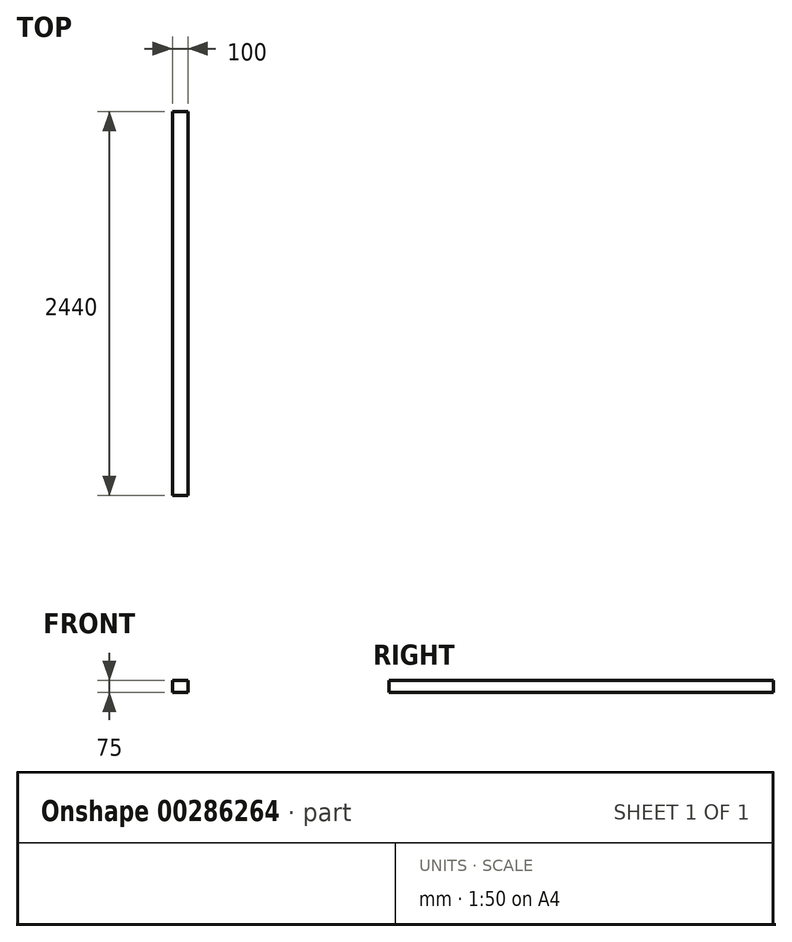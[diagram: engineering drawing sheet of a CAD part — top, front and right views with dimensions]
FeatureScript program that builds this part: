
annotation { "Feature Type Name" : "Feature", "Feature Type Description" : "" }
export const myFeature = defineFeature(function(context is Context, id is Id, definition is map)
    precondition{}
    {
        {
            var Q0;
            Q0=qCreatedBy(makeId("Front.planeOp"),FACE);
            var sketch = newSketch(context, id + "F0", { "sketchPlane" : qUnion([Q0])});
            skLineSegment(sketch, "E0.bottom", {"start": v(-50, 37.5) * mm, "end": v(50, 37.5) * mm});
            skLineSegment(sketch, "E0.top", {"start": v(-50, -37.5) * mm, "end": v(50, -37.5) * mm});
            skLineSegment(sketch, "E0.left", {"start": v(-50, 37.5) * mm, "end": v(-50, -37.5) * mm});
            skLineSegment(sketch, "E0.right", {"start": v(50, 37.5) * mm, "end": v(50, -37.5) * mm});
            skSolve(sketch);
        }
        {
            var Q0;
            Q0=makeQuery(id+"F0.imprint","IMPRINT",FACE,{"disambiguationData":[TD([[makeQuery(id+"F0.imprint","IMPRINT",EDGE,{"derivedFrom":sQuery(id+"F0.wireOp",EDGE,"E0.bottom")}),-1.0]])]});
            extrude(context, id + "F1", {"entities" : qUnion([Q0]), "depth" : 2440 * mm});
        }
    });
